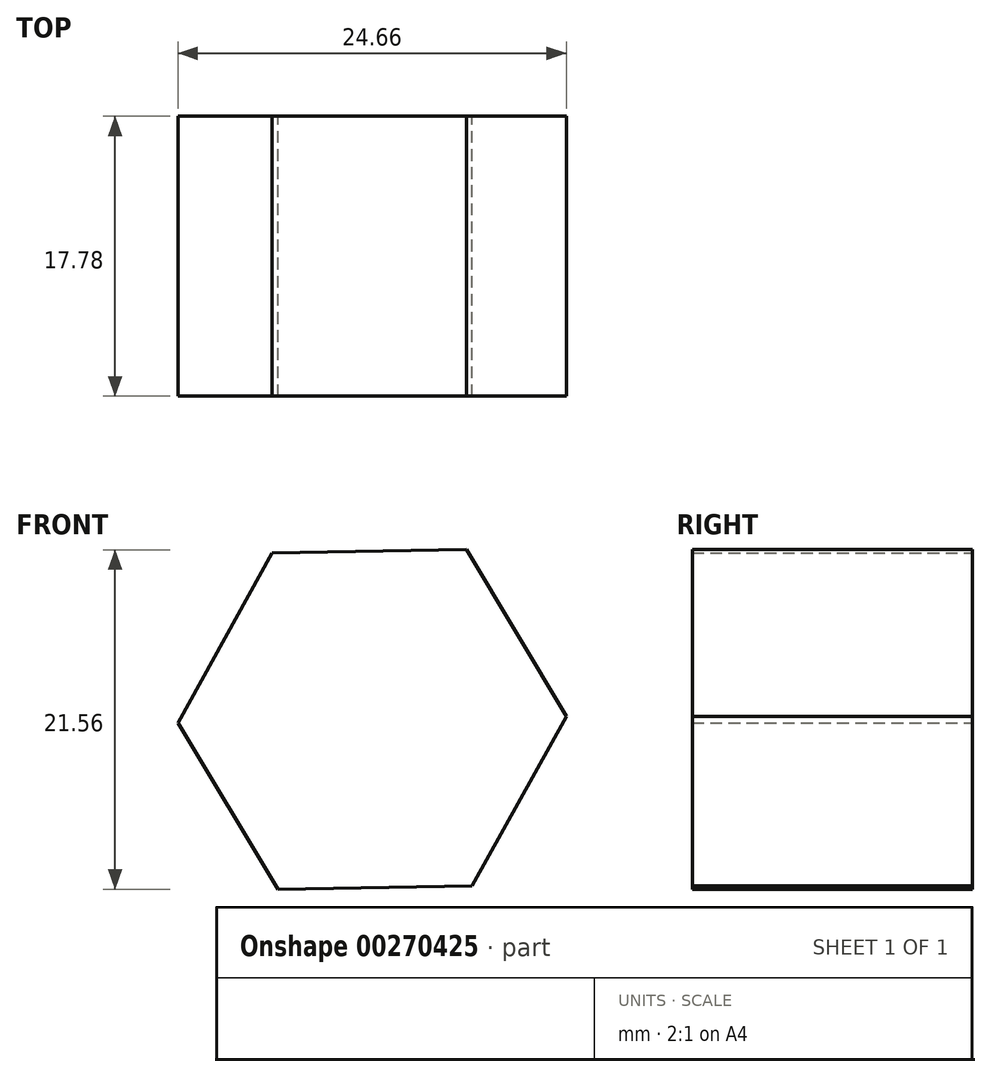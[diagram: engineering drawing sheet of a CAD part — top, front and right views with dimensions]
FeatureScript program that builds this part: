
annotation { "Feature Type Name" : "Feature", "Feature Type Description" : "" }
export const myFeature = defineFeature(function(context is Context, id is Id, definition is map)
    precondition{}
    {
        {
            var Q0;
            Q0=qCreatedBy(makeId("Front.planeOp"),FACE);
            var sketch = newSketch(context, id + "F0", { "sketchPlane" : qUnion([Q0])});
            skCircle(sketch, "E0.cCircle", {"center": v(0, 0) * mm, "radius": 10.68 * mm, "construction": true});
            skLineSegment(sketch, "E0.0", {"start": v(5.99, 10.78) * mm, "end": v(12.33, 0.2) * mm});
            skLineSegment(sketch, "E0.1", {"start": v(12.33, 0.2) * mm, "end": v(6.34, -10.57) * mm});
            skLineSegment(sketch, "E0.2", {"start": v(6.34, -10.57) * mm, "end": v(-5.99, -10.78) * mm});
            skLineSegment(sketch, "E0.3", {"start": v(-5.99, -10.78) * mm, "end": v(-12.33, -0.2) * mm});
            skLineSegment(sketch, "E0.4", {"start": v(-12.33, -0.2) * mm, "end": v(-6.34, 10.57) * mm});
            skLineSegment(sketch, "E0.5", {"start": v(-6.34, 10.57) * mm, "end": v(5.99, 10.78) * mm});
            skPoint(sketch, "E0.0.midPoint", {"position": v(9.16, 5.5) * mm});
            skSolve(sketch);
        }
        {
            var Q0;
            Q0=qCreatedBy(makeId("Top.planeOp"),FACE);
            var sketch = newSketch(context, id + "F1", { "sketchPlane" : qUnion([Q0])});
            skLineSegment(sketch, "E1", {"start": v(0, 0) * mm, "end": v(0, 17.78) * mm});
            skSolve(sketch);
        }
        {
            var Q0;
            Q0=makeQuery(id+"F0.imprint","IMPRINT",FACE,{"disambiguationData":[TD([[makeQuery(id+"F0.imprint","IMPRINT",EDGE,{"derivedFrom":sQuery(id+"F0.wireOp",EDGE,"E0.0")}),-1.0]])]});
            var Q1;
            Q1=sQuery(id+"F1.wireOp",EDGE,"E1");
            sweep(context, id + "F2", {"profiles" : qUnion([Q0]), "path" : qUnion([Q1])});
        }
    });
